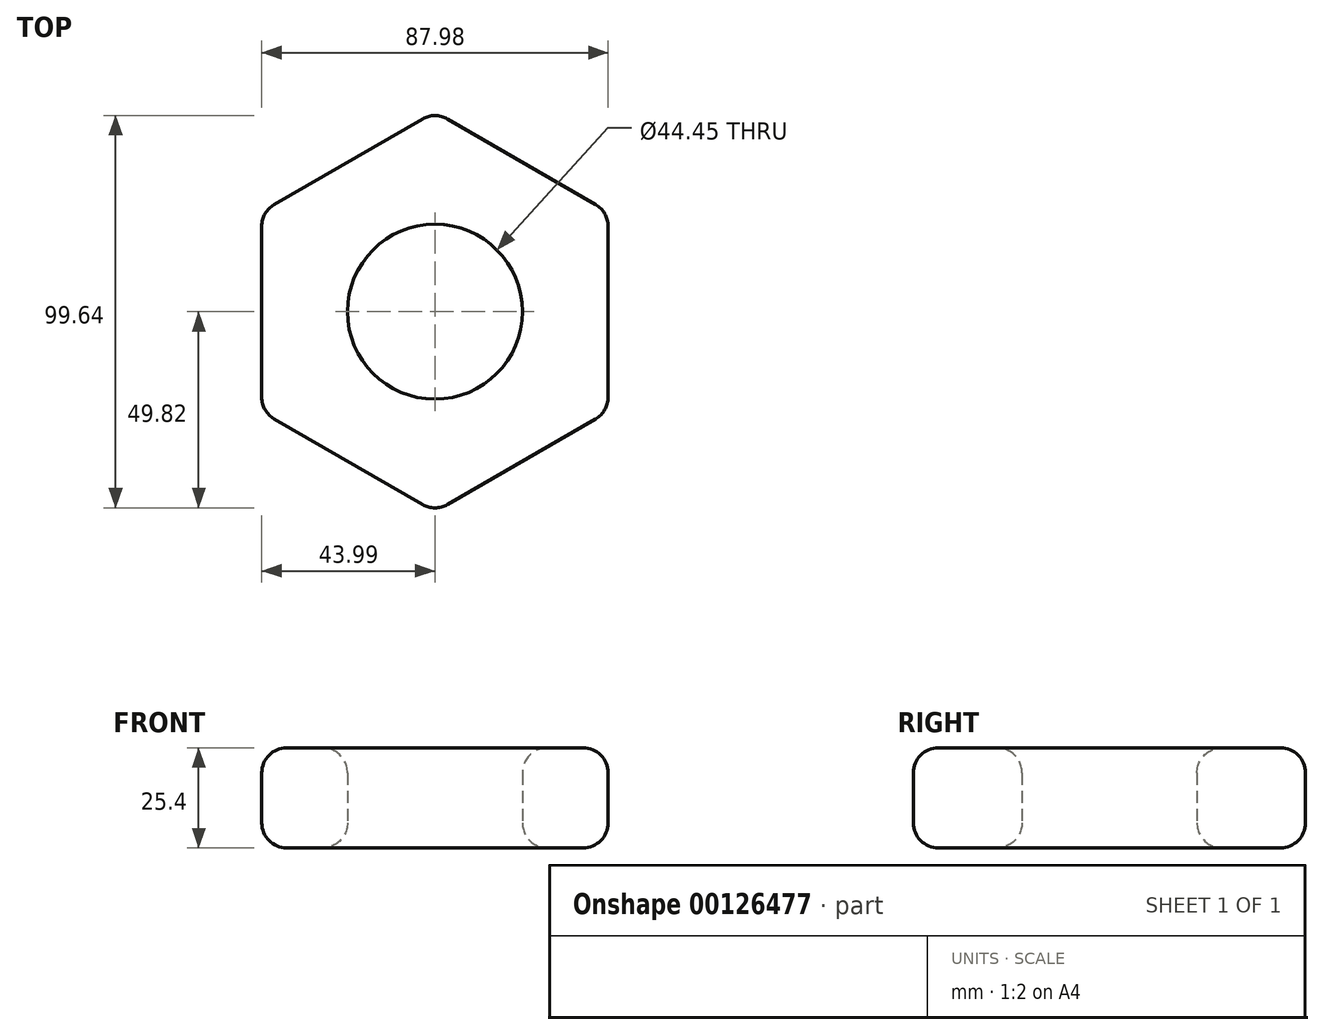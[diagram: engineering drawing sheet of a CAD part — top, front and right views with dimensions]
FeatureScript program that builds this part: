
annotation { "Feature Type Name" : "Feature", "Feature Type Description" : "" }
export const myFeature = defineFeature(function(context is Context, id is Id, definition is map)
    precondition{}
    {
        {
            var Q0;
            Q0=qCreatedBy(makeId("Top.planeOp"),FACE);
            var sketch = newSketch(context, id + "F0", { "sketchPlane" : qUnion([Q0])});
            skCircle(sketch, "E0.cCircle", {"center": v(0, 0) * mm, "radius": 50.8 * mm, "construction": true});
            skLineSegment(sketch, "E0.0", {"start": v(44, -25.4) * mm, "end": v(0, -50.8) * mm});
            skLineSegment(sketch, "E0.1", {"start": v(0, -50.8) * mm, "end": v(-44, -25.4) * mm});
            skLineSegment(sketch, "E0.2", {"start": v(-44, -25.4) * mm, "end": v(-44, 25.4) * mm});
            skLineSegment(sketch, "E0.3", {"start": v(-44, 25.4) * mm, "end": v(0, 50.8) * mm});
            skLineSegment(sketch, "E0.4", {"start": v(0, 50.8) * mm, "end": v(44, 25.4) * mm});
            skLineSegment(sketch, "E0.5", {"start": v(44, 25.4) * mm, "end": v(44, -25.4) * mm});
            skCircle(sketch, "E1", {"center": v(0, 0) * mm, "radius": 22.23 * mm});
            skSolve(sketch);
        }
        {
            var Q0;
            Q0=makeQuery(id+"F0.imprint","IMPRINT",FACE,{"disambiguationData":[TD([[makeQuery(id+"F0.imprint","IMPRINT",EDGE,{"derivedFrom":sQuery(id+"F0.wireOp",EDGE,"E0.0")}),-1.0]])]});
            extrude(context, id + "F1", {"entities" : qUnion([Q0]), "depth" : 25.4 * mm});
        }
        {
            var Q0;
            Q0=makeQuery(id+"F1.opExtrude","SWEPT_EDGE",EDGE,{"disambiguationData":[OSD([sQuery(id+"F0.wireOp",EDGE,"E0.1"),sQuery(id+"F0.wireOp",EDGE,"E0.2")])]});
            var Q1;
            Q1=makeQuery(id+"F1.opExtrude","SWEPT_EDGE",EDGE,{"disambiguationData":[OSD([sQuery(id+"F0.wireOp",EDGE,"E0.2"),sQuery(id+"F0.wireOp",EDGE,"E0.3")])]});
            var Q2;
            Q2=makeQuery(id+"F1.opExtrude","SWEPT_EDGE",EDGE,{"disambiguationData":[OSD([sQuery(id+"F0.wireOp",EDGE,"E0.0"),sQuery(id+"F0.wireOp",EDGE,"E0.1")])]});
            var Q3;
            Q3=makeQuery(id+"F1.opExtrude","SWEPT_EDGE",EDGE,{"disambiguationData":[OSD([sQuery(id+"F0.wireOp",EDGE,"E0.0"),sQuery(id+"F0.wireOp",EDGE,"E0.5")])]});
            var Q4;
            Q4=makeQuery(id+"F1.opExtrude","SWEPT_EDGE",EDGE,{"disambiguationData":[OSD([sQuery(id+"F0.wireOp",EDGE,"E0.4"),sQuery(id+"F0.wireOp",EDGE,"E0.5")])]});
            var Q5;
            Q5=makeQuery(id+"F1.opExtrude","SWEPT_EDGE",EDGE,{"disambiguationData":[OSD([sQuery(id+"F0.wireOp",EDGE,"E0.3"),sQuery(id+"F0.wireOp",EDGE,"E0.4")])]});
            fillet(context, id + "F2", {"entities" : qUnion([Q0, Q1, Q2, Q3, Q4, Q5]), "radius" : 6.35 * mm, "tangentPropagation" : true, "allowEdgeOverflow" : false});
        }
        {
            var Q0;
            Q0=makeQuery(id+"F1.opExtrude","CAP_EDGE",EDGE,{"disambiguationData":[OSD([sQuery(id+"F0.wireOp",EDGE,"byHo3bf8-m2aO-Knk7-fECa-O3aBIwqKxkP6.bottom")])],"isStart":false});
            var Q1;
            Q1=makeQuery(id+"F1.opExtrude","CAP_EDGE",EDGE,{"disambiguationData":[OSD([sQuery(id+"F0.wireOp",EDGE,"byHo3bf8-m2aO-Knk7-fECa-O3aBIwqKxkP6.bottom")])],"isStart":true});
            var Q2;
            Q2=makeQuery(id+"F1.opExtrude","CAP_EDGE",EDGE,{"disambiguationData":[OSD([sQuery(id+"F0.wireOp",EDGE,"hhzElSMt-TSmA-8YAS-kCnB-v2NUc7en6oYG")])],"isStart":false});
            var Q3;
            Q3=makeQuery(id+"F1.opExtrude","CAP_EDGE",EDGE,{"disambiguationData":[OSD([sQuery(id+"F0.wireOp",EDGE,"hhzElSMt-TSmA-8YAS-kCnB-v2NUc7en6oYG")])],"isStart":true});
            var Q4;
            Q4=makeQuery(id+"F1.opExtrude","CAP_EDGE",EDGE,{"disambiguationData":[OSD([sQuery(id+"F0.wireOp",EDGE,"E0.1")])],"isStart":false});
            var Q5;
            Q5=makeQuery(id+"F1.opExtrude","CAP_EDGE",EDGE,{"disambiguationData":[OSD([sQuery(id+"F0.wireOp",EDGE,"E0.1")])],"isStart":true});
            var Q6;
            Q6=makeQuery(id+"F1.opExtrude","CAP_EDGE",EDGE,{"disambiguationData":[OSD([sQuery(id+"F0.wireOp",EDGE,"E1")])],"isStart":false});
            var Q7;
            Q7=makeQuery(id+"F1.opExtrude","CAP_EDGE",EDGE,{"disambiguationData":[OSD([sQuery(id+"F0.wireOp",EDGE,"E1")])],"isStart":true});
            fillet(context, id + "F3", {"entities" : qUnion([Q0, Q1, Q2, Q3, Q4, Q5, Q6, Q7]), "radius" : 6.35 * mm, "tangentPropagation" : true, "allowEdgeOverflow" : false});
        }
    });
